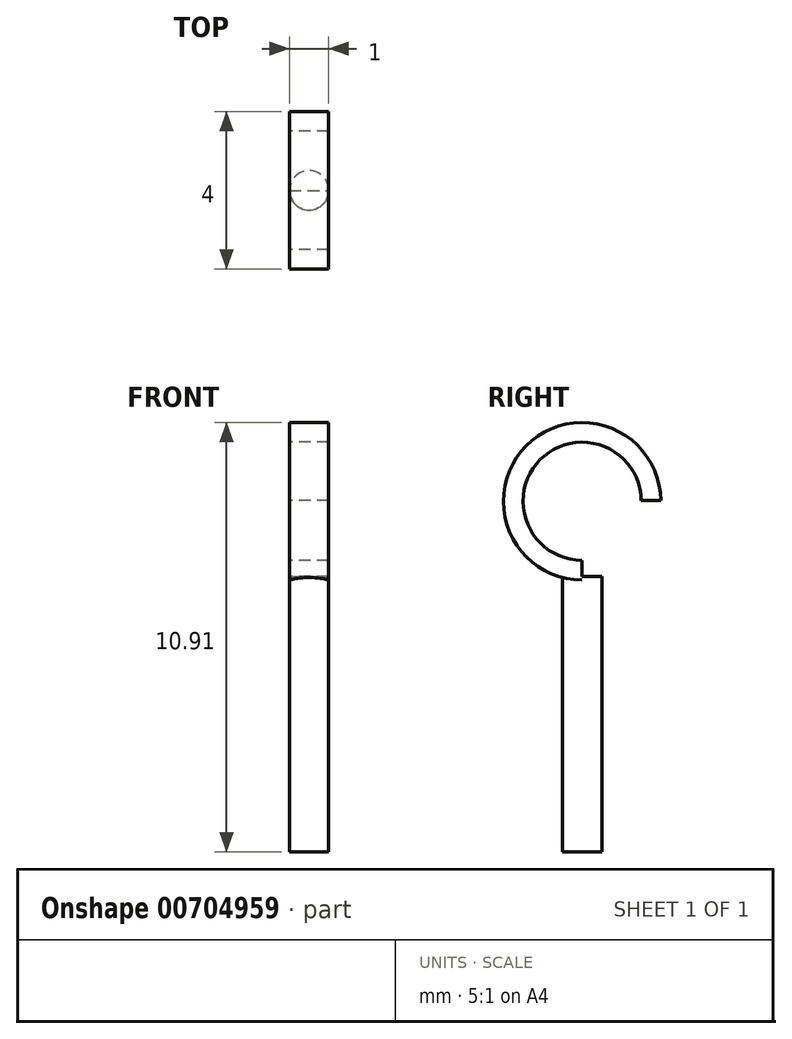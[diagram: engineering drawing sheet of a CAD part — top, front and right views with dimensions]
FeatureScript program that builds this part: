
annotation { "Feature Type Name" : "Feature", "Feature Type Description" : "" }
export const myFeature = defineFeature(function(context is Context, id is Id, definition is map)
    precondition{}
    {
        {
            var Q0;
            Q0=qCreatedBy(makeId("Top.planeOp"),FACE);
            var sketch = newSketch(context, id + "F0", { "sketchPlane" : qUnion([Q0])});
            skCircle(sketch, "E0", {"center": v(0, 0) * mm, "radius": 0.5 * mm});
            skSolve(sketch);
        }
        {
            var Q0;
            Q0 = qSketchRegion(id + "F0", true);
            extrude(context, id + "F1", {"entities" : qUnion([Q0]), "depth" : 7 * mm, "offsetDistance" : 25 * mm});
        }
        {
            var Q0;
            Q0=qCreatedBy(makeId("Right.planeOp"),FACE);
            var sketch = newSketch(context, id + "F2", { "sketchPlane" : qUnion([Q0])});
            skCircle(sketch, "E1", {"center": v(0, 8.91) * mm, "radius": 2 * mm});
            skCircle(sketch, "E2", {"center": v(0, 8.91) * mm, "radius": 1.5 * mm});
            skLineSegment(sketch, "E3", {"start": v(1.5, 8.93) * mm, "end": v(2, 8.93) * mm});
            skLineSegment(sketch, "E4", {"start": v(0, 6.91) * mm, "end": v(0, 7.41) * mm});
            skSolve(sketch);
        }
        {
            var Q0;
            {var subQ0=sQuery(id+"F2.wireOp",EDGE,"E3");Q0=makeQuery(id+"F2.imprint","IMPRINT",FACE,{"disambiguationData":[TD([[makeQuery(id+"F2.imprint","IMPRINT",EDGE,{"derivedFrom":subQ0}),1.0]])]});}
            extrude(context, id + "F3", {"entities" : qUnion([Q0]), "operationType" : NewBodyOperationType.ADD, "endBound" : BoundingType.SYMMETRIC, "depth" : 1 * mm, "offsetDistance" : 25 * mm});
        }
    });
